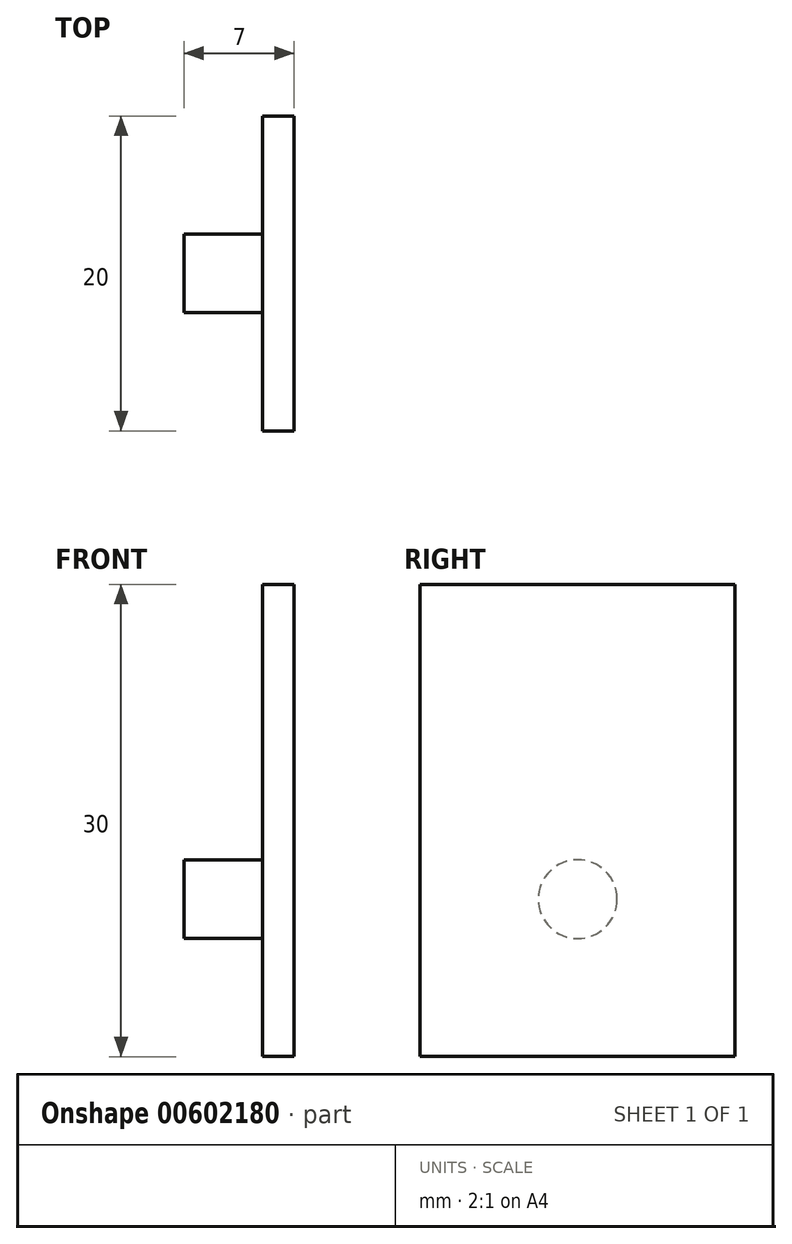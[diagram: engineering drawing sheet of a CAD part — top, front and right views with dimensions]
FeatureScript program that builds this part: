
annotation { "Feature Type Name" : "Feature", "Feature Type Description" : "" }
export const myFeature = defineFeature(function(context is Context, id is Id, definition is map)
    precondition{}
    {
        {
            var Q0;
            Q0=qCreatedBy(makeId("Right.planeOp"),FACE);
            var sketch = newSketch(context, id + "F0", { "sketchPlane" : qUnion([Q0])});
            skLineSegment(sketch, "E0.bottom", {"start": v(-41.92, 24.56) * mm, "end": v(-21.92, 24.56) * mm});
            skLineSegment(sketch, "E0.top", {"start": v(-41.92, 4.56) * mm, "end": v(-21.92, 4.56) * mm});
            skLineSegment(sketch, "E0.left", {"start": v(-41.92, 24.56) * mm, "end": v(-41.92, 4.56) * mm});
            skLineSegment(sketch, "E0.right", {"start": v(-21.92, 24.56) * mm, "end": v(-21.92, 4.56) * mm});
            skLineSegment(sketch, "E1", {"start": v(-41.92, 24.56) * mm, "end": v(-21.92, 4.56) * mm});
            skLineSegment(sketch, "E2", {"start": v(-21.92, 24.56) * mm, "end": v(-41.92, 4.56) * mm});
            skCircle(sketch, "E3", {"center": v(-31.92, 14.56) * mm, "radius": 2.5 * mm});
            skSolve(sketch);
        }
        {
            var Q0;
            Q0 = qSketchRegion(id + "F0", true);
            var Q1;
            {var subQ0=sQuery(id+"F0.wireOp",EDGE,"E0.bottom");Q1=makeQuery(id+"F0.imprint","IMPRINT",FACE,{"disambiguationData":[TD([[makeQuery(id+"F0.imprint","IMPRINT",EDGE,{"derivedFrom":subQ0}),-1.0]])]});}
            var Q2;
            {var subQ0=sQuery(id+"F0.wireOp",EDGE,"E3");var subQ1=sQuery(id+"F0.wireOp",EDGE,"E1");var subQ2=makeQuery(id+"F0.imprint","INTERSECT",VERTEX,{"disambiguationData":[OD(0.0)],"derivedFrom":[subQ1,subQ0]});Q2=makeQuery(id+"F0.imprint","IMPRINT",FACE,{"disambiguationData":[TD([[makeQuery(id+"F0.imprint","IMPRINT",EDGE,{"disambiguationData":[TD([[subQ2,-1.0]])],"derivedFrom":subQ1}),-1.0]])]});}
            var Q3;
            {var subQ0=sQuery(id+"F0.wireOp",EDGE,"E3");var subQ1=sQuery(id+"F0.wireOp",EDGE,"E1");var subQ2=makeQuery(id+"F0.imprint","INTERSECT",VERTEX,{"disambiguationData":[OD(0.0)],"derivedFrom":[subQ1,subQ0]});Q3=makeQuery(id+"F0.imprint","IMPRINT",FACE,{"disambiguationData":[TD([[makeQuery(id+"F0.imprint","IMPRINT",EDGE,{"disambiguationData":[TD([[subQ2,-1.0]])],"derivedFrom":subQ1}),1.0]])]});}
            var Q4;
            {var subQ0=sQuery(id+"F0.wireOp",EDGE,"E2");var subQ1=sQuery(id+"F0.wireOp",EDGE,"E1");var subQ2=makeQuery(id+"F0.imprint","INTERSECT",VERTEX,{"derivedFrom":[subQ1,subQ0]});Q4=makeQuery(id+"F0.imprint","IMPRINT",FACE,{"disambiguationData":[TD([[makeQuery(id+"F0.imprint","IMPRINT",EDGE,{"disambiguationData":[TD([[subQ2,-1.0]])],"derivedFrom":subQ1}),1.0]])]});}
            var Q5;
            {var subQ0=sQuery(id+"F0.wireOp",EDGE,"E2");var subQ1=sQuery(id+"F0.wireOp",EDGE,"E1");var subQ2=makeQuery(id+"F0.imprint","INTERSECT",VERTEX,{"derivedFrom":[subQ1,subQ0]});Q5=makeQuery(id+"F0.imprint","IMPRINT",FACE,{"disambiguationData":[TD([[makeQuery(id+"F0.imprint","IMPRINT",EDGE,{"disambiguationData":[TD([[subQ2,-1.0]])],"derivedFrom":subQ1}),-1.0]])]});}
            extrude(context, id + "F1", {"entities" : qUnion([Q0, Q1, Q2, Q3, Q4, Q5]), "depth" : 2 * mm, "offsetDistance" : 25 * mm});
        }
        {
            var Q0;
            {var subQ0=sQuery(id+"F0.wireOp",EDGE,"E2");var subQ1=sQuery(id+"F0.wireOp",EDGE,"E1");var subQ2=makeQuery(id+"F0.imprint","INTERSECT",VERTEX,{"derivedFrom":[subQ1,subQ0]});Q0=makeQuery(id+"F0.imprint","IMPRINT",FACE,{"disambiguationData":[TD([[makeQuery(id+"F0.imprint","IMPRINT",EDGE,{"disambiguationData":[TD([[subQ2,-1.0]])],"derivedFrom":subQ1}),1.0]])]});}
            var Q1;
            {var subQ0=sQuery(id+"F0.wireOp",EDGE,"E3");var subQ1=sQuery(id+"F0.wireOp",EDGE,"E1");var subQ2=makeQuery(id+"F0.imprint","INTERSECT",VERTEX,{"disambiguationData":[OD(0.0)],"derivedFrom":[subQ1,subQ0]});Q1=makeQuery(id+"F0.imprint","IMPRINT",FACE,{"disambiguationData":[TD([[makeQuery(id+"F0.imprint","IMPRINT",EDGE,{"disambiguationData":[TD([[subQ2,-1.0]])],"derivedFrom":subQ1}),1.0]])]});}
            var Q2;
            {var subQ0=sQuery(id+"F0.wireOp",EDGE,"E3");var subQ1=sQuery(id+"F0.wireOp",EDGE,"E1");var subQ2=makeQuery(id+"F0.imprint","INTERSECT",VERTEX,{"disambiguationData":[OD(0.0)],"derivedFrom":[subQ1,subQ0]});Q2=makeQuery(id+"F0.imprint","IMPRINT",FACE,{"disambiguationData":[TD([[makeQuery(id+"F0.imprint","IMPRINT",EDGE,{"disambiguationData":[TD([[subQ2,-1.0]])],"derivedFrom":subQ1}),-1.0]])]});}
            var Q3;
            {var subQ0=sQuery(id+"F0.wireOp",EDGE,"E2");var subQ1=sQuery(id+"F0.wireOp",EDGE,"E1");var subQ2=makeQuery(id+"F0.imprint","INTERSECT",VERTEX,{"derivedFrom":[subQ1,subQ0]});Q3=makeQuery(id+"F0.imprint","IMPRINT",FACE,{"disambiguationData":[TD([[makeQuery(id+"F0.imprint","IMPRINT",EDGE,{"disambiguationData":[TD([[subQ2,-1.0]])],"derivedFrom":subQ1}),-1.0]])]});}
            extrude(context, id + "F2", {"entities" : qUnion([Q0, Q1, Q2, Q3]), "operationType" : NewBodyOperationType.ADD, "oppositeDirection" : true, "depth" : 5 * mm, "offsetDistance" : 25 * mm});
        }
        {
            var Q0;
            Q0=makeQuery(id+"F1.opExtrude","SWEPT_FACE",FACE,{"disambiguationData":[OSD([sQuery(id+"F0.wireOp",EDGE,"E0.bottom")])]});
            extrude(context, id + "F3", {"entities" : qUnion([Q0]), "operationType" : NewBodyOperationType.ADD, "depth" : 10 * mm, "offsetDistance" : 25 * mm});
        }
    });
